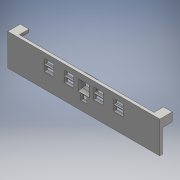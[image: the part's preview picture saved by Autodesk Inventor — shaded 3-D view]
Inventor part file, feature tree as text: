
AUTODESK INVENTOR PART (.ipt)
format: ipt  version: 2016 (Build 200138000, 138)  size: 232,448 bytes
history: native  units: mm
features: extrude x6, sketch x6, chamfer x3, pattern_linear x2
ambient origin geometry x8: Origin, YZ Plane, XZ Plane, XY Plane, X Axis, Y Axis, Z Axis, Center Point
bodies: Solid1 (feature_tree)
feature tree (17):
  extrude  "Extrusion1"  Depth=11.0mm
  extrude  "walls"  Depth=3.0mm
  extrude  "Extrusion2"  TaperAngle=0.0deg  [1 undecoded]
  extrude  "lineSensorHole"  Depth=1.5mm TaperAngle=0.0deg
  chamfer  "Chamfer2"  Distance=0.4mm
  chamfer  "Chamfer3"  Distance=1.5mm
  pattern_linear  "Rectangular Pattern3"  Spacing1=0.875mm  [1 undecoded]
  extrude  "colorSensorHole"  Depth=0.5mm
  extrude  "Extrusion5"  Depth=0.5mm
  pattern_linear  "Rectangular Pattern4"  Spacing1=0.5mm  [1 undecoded]
  chamfer  "Chamfer4"  Distance=0.5mm
  sketch  "Sketch1"  dims[d0=52.5mm d1=11.0mm]
  sketch  "Sketch2"  dims[d2=1.0mm d3=0.0mm d5=3.0mm]
  sketch  "Sketch3"  dims[d8=5.0mm d10=0.0mm]
  sketch  "Sketch4"  dims[d12=3.2mm d13=1.5mm d14=0.0mm]
  sketch  "Sketch5"  dims[d15=1.7mm]
  sketch  "Sketch6"  dims[d16=1.7mm d17=0.4mm d25=1.5mm d26=0.0mm d34=0.875mm d35=0.5mm d36=0.5mm d37=0.5mm d38=0.5mm d39=1.6mm d40=0.0mm d41=1.0mm d43=1.0mm d44=3.3mm d45=0.0mm d46=3.0mm d47=3.0mm d48=11.7mm d49=23.375mm d61=2.0mm d63=0.5mm d64=2.0mm d65=1.745329mm d66=20.0mm d68=6.95mm d69=0.8mm d70=20.0mm d72=17.0mm d75=1.4mm d76=2.0mm d77=15.0deg d83=2.0mm d85=2.0mm d86=6.48mm d87=5.44mm d88=3.87mm d89=1.5mm d90=0.5mm d91=0.5mm d92=0.5mm d93=0.5mm]
note: 3 required parameter values undecoded (feature->parameter linkage not recoverable at this tier; creation-order binding heuristic only, values carry confidence <= 0.55)
